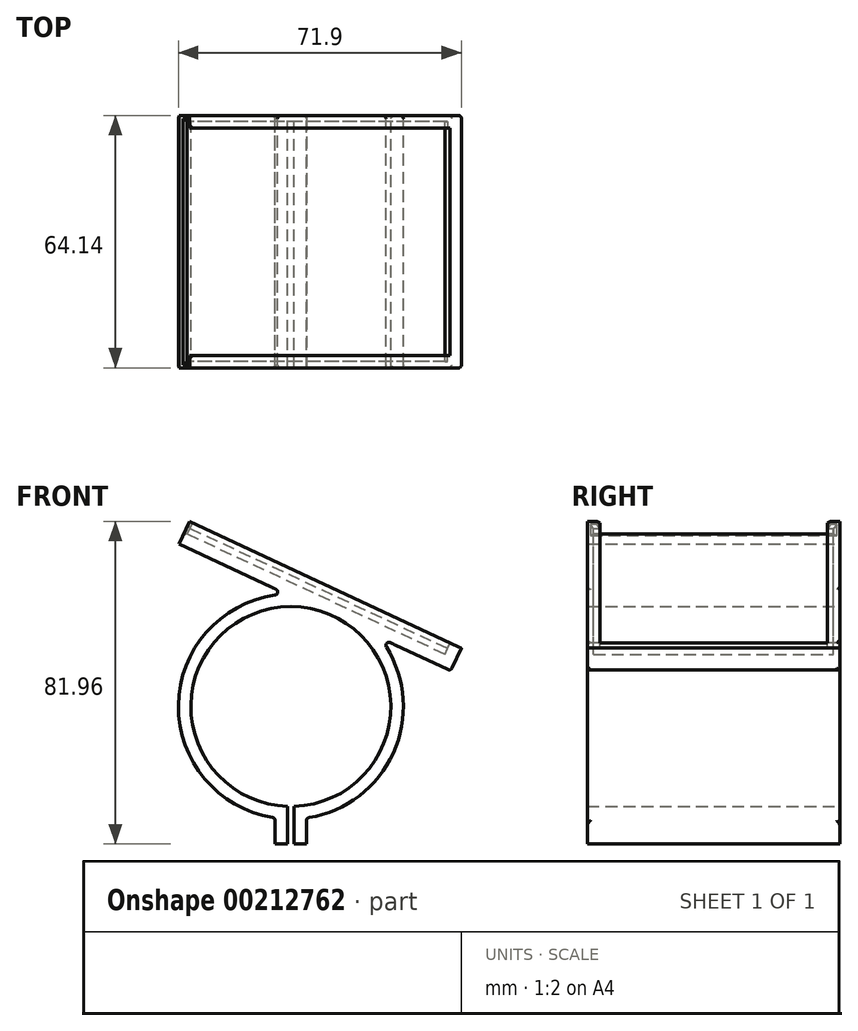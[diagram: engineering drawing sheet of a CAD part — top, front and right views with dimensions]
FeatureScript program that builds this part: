
annotation { "Feature Type Name" : "Feature", "Feature Type Description" : "" }
export const myFeature = defineFeature(function(context is Context, id is Id, definition is map)
    precondition{}
    {
        {
            var Q0;
            Q0=qCreatedBy(makeId("Front.planeOp"),FACE);
            var sketch = newSketch(context, id + "F0", { "sketchPlane" : qUnion([Q0])});
            skArc(sketch, "E0", {"start": v(0.8, -25.39) * mm, "mid": v(0, 25.4) * mm, "end": v(-0.8, -25.39) * mm});
            skArc(sketch, "E1.0", {"start": v(0.8, -28.56) * mm, "mid": v(0, 28.58) * mm, "end": v(-0.8, -28.56) * mm});
            skLineSegment(sketch, "E2", {"start": v(0, 0) * mm, "end": v(67.61, 0) * mm, "construction": true});
            skLineSegment(sketch, "E3", {"start": v(67.61, 0) * mm, "end": v(-41.32, 50.8) * mm, "construction": true});
            skLineSegment(sketch, "E4.0", {"start": v(40.65, 9.07) * mm, "end": v(-28.41, 41.27) * mm});
            skLineSegment(sketch, "E5", {"start": v(-28.41, 41.28) * mm, "end": v(-27.07, 44.15) * mm});
            skLineSegment(sketch, "E6", {"start": v(40.65, 9.07) * mm, "end": v(41.99, 11.95) * mm});
            skLineSegment(sketch, "E7", {"start": v(41.99, 11.95) * mm, "end": v(-27.07, 44.15) * mm});
            skLineSegment(sketch, "E8", {"start": v(0, 0) * mm, "end": v(0, -34.93) * mm, "construction": true});
            skLineSegment(sketch, "E9.0", {"start": v(0.8, 0) * mm, "end": v(0.8, -34.93) * mm});
            skLineSegment(sketch, "E10", {"start": v(0, -34.93) * mm, "end": v(0.8, -34.93) * mm, "construction": true});
            skLineSegment(sketch, "E11", {"start": v(0.8, -34.93) * mm, "end": v(3.97, -34.93) * mm});
            skLineSegment(sketch, "E12", {"start": v(3.97, -34.93) * mm, "end": v(3.97, -28.3) * mm});
            skLineSegment(sketch, "E13", {"start": v(0.8, -34.93) * mm, "end": v(0.8, -25.39) * mm, "construction": true});
            skLineSegment(sketch, "E14.MirrorCS", {"start": v(-0.8, 0) * mm, "end": v(-0.8, -34.93) * mm});
            skLineSegment(sketch, "E15.MirrorCS", {"start": v(-0.8, -34.93) * mm, "end": v(-3.97, -34.93) * mm});
            skLineSegment(sketch, "E16.MirrorCS", {"start": v(-0.8, -34.93) * mm, "end": v(-0.8, -25.39) * mm, "construction": true});
            skLineSegment(sketch, "E17.MirrorCS", {"start": v(0, -34.93) * mm, "end": v(-0.8, -34.93) * mm, "construction": true});
            skLineSegment(sketch, "E18.MirrorCS", {"start": v(-3.97, -34.93) * mm, "end": v(-3.97, -28.3) * mm});
            skSolve(sketch);
        }
        {
            var Q0;
            Q0 = qSketchRegion(id + "F0", true);
            extrude(context, id + "F1", {"entities" : qUnion([Q0]), "depth" : 64.13 * mm, "offsetDistance" : 25.4 * mm});
        }
        {
            var Q0;
            Q0=makeQuery(id+"F1.opExtrude","SWEPT_FACE",FACE,{"disambiguationData":[OSD([sQuery(id+"F0.wireOp",EDGE,"E5")])]});
            var sketch = newSketch(context, id + "F2", { "sketchPlane" : qUnion([Q0])});
            skLineSegment(sketch, "E19", {"start": v(0, 28.58) * mm, "end": v(0, 31.75) * mm});
            skLineSegment(sketch, "E20", {"start": v(0, 31.75) * mm, "end": v(3.18, 31.75) * mm});
            skLineSegment(sketch, "E21", {"start": v(3.18, 31.75) * mm, "end": v(3.18, 30.16) * mm});
            skLineSegment(sketch, "E22", {"start": v(3.18, 30.16) * mm, "end": v(1.59, 30.16) * mm});
            skPoint(sketch, "E22.endSnap0", {"position": v(1.59, 31.75) * mm});
            skLineSegment(sketch, "E23", {"start": v(1.59, 30.16) * mm, "end": v(1.59, 28.58) * mm});
            skLineSegment(sketch, "E24", {"start": v(32.07, 28.58) * mm, "end": v(32.07, 32.24) * mm, "construction": true});
            skLineSegment(sketch, "E25.MirrorCS", {"start": v(62.55, 30.16) * mm, "end": v(62.55, 28.58) * mm});
            skLineSegment(sketch, "E26.MirrorCS", {"start": v(64.13, 31.75) * mm, "end": v(60.96, 31.75) * mm});
            skPoint(sketch, "E27.MirrorP", {"position": v(62.55, 31.75) * mm});
            skLineSegment(sketch, "E28.MirrorCS", {"start": v(60.96, 30.16) * mm, "end": v(62.55, 30.16) * mm});
            skLineSegment(sketch, "E29.MirrorCS", {"start": v(60.96, 31.75) * mm, "end": v(60.96, 30.16) * mm});
            skLineSegment(sketch, "E30.MirrorCS", {"start": v(64.13, 28.58) * mm, "end": v(64.13, 31.75) * mm});
            skSolve(sketch);
        }
        {
            var Q0;
            {var subQ0=sQuery(id+"F2.wireOp",EDGE,"E19");Q0=makeQuery(id+"F2.imprint","IMPRINT",FACE,{"disambiguationData":[TD([[makeQuery(id+"F2.imprint","IMPRINT",EDGE,{"derivedFrom":subQ0}),-1.0]])]});}
            var Q1;
            {var subQ0=sQuery(id+"F2.wireOp",EDGE,"E25.MirrorCS");Q1=makeQuery(id+"F2.imprint","IMPRINT",FACE,{"disambiguationData":[TD([[makeQuery(id+"F2.imprint","IMPRINT",EDGE,{"derivedFrom":subQ0}),1.0]])]});}
            var Q2;
            Q2=makeQuery(id+"F1.opExtrude","SWEPT_FACE",FACE,{"disambiguationData":[OSD([sQuery(id+"F0.wireOp",EDGE,"E6")])]});
            extrude(context, id + "F3", {"entities" : qUnion([Q0, Q1]), "operationType" : NewBodyOperationType.ADD, "endBound" : BoundingType.UP_TO_SURFACE, "oppositeDirection" : true, "depth" : 25.4 * mm, "endBoundEntityFace" : qUnion([Q2]), "offsetDistance" : 25.4 * mm});
        }
        {
            var Q0;
            {var subQ0=sQuery(id+"F0.wireOp",EDGE,"E6");Q0=makeQuery(id+"F3.boolean.opBoolean","MERGE",FACE,{"derivedFrom":[makeQuery(id+"F1.opExtrude","SWEPT_FACE",FACE,{"disambiguationData":[OSD([subQ0])]}),makeQuery(id+"F3.opExtrude","CAP_FACE",FACE,{"disambiguationData":[OSD([subQ0]),OD(0.0)],"isStart":false}),makeQuery(id+"F3.opExtrude","CAP_FACE",FACE,{"disambiguationData":[OSD([subQ0]),OD(1.0)],"isStart":false})]});}
            var sketch = newSketch(context, id + "F4", { "sketchPlane" : qUnion([Q0])});
            skLineSegment(sketch, "E31", {"start": v(-60.96, 31.75) * mm, "end": v(-3.18, 31.75) * mm});
            skSolve(sketch);
        }
        {
            var Q0;
            Q0=makeQuery(id+"F4.imprint","IMPRINT",FACE,{"disambiguationData":[TD([[makeQuery(id+"F4.imprint","IMPRINT",EDGE,{"derivedFrom":sQuery(id+"F4.wireOp",EDGE,"E31")}),-1.0]])]});
            extrude(context, id + "F5", {"entities" : qUnion([Q0]), "operationType" : NewBodyOperationType.ADD, "oppositeDirection" : true, "depth" : 3.17 * mm, "offsetDistance" : 25.4 * mm});
        }
        {
            var Q0;
            {var subQ0=sQuery(id+"F0.wireOp",EDGE,"E1.0");Q0=makeQuery(id+"F1.opExtrude","CAP_EDGE",EDGE,{"disambiguationData":[OSD([subQ0]),TDD([makeQuery(id+"F0.imprint","IMPRINT",EDGE,{"disambiguationData":[TD([[makeQuery(id+"F0.imprint","INTERSECT",VERTEX,{"derivedFrom":[subQ0,sQuery(id+"F0.wireOp",EDGE,"E18.MirrorCS")]}),1.0]])],"derivedFrom":subQ0})])],"isStart":true});}
            var Q1;
            {var subQ0=sQuery(id+"F0.wireOp",EDGE,"E1.0");Q1=makeQuery(id+"F1.opExtrude","CAP_EDGE",EDGE,{"disambiguationData":[OSD([subQ0]),TDD([makeQuery(id+"F0.imprint","IMPRINT",EDGE,{"disambiguationData":[TD([[makeQuery(id+"F0.imprint","INTERSECT",VERTEX,{"derivedFrom":[subQ0,sQuery(id+"F0.wireOp",EDGE,"E18.MirrorCS")]}),1.0]])],"derivedFrom":subQ0})])],"isStart":false});}
            var Q2;
            {var subQ0=sQuery(id+"F0.wireOp",EDGE,"E4.0");var subQ1=sQuery(id+"F0.wireOp",EDGE,"E1.0");Q2=makeQuery(id+"F1.opExtrude","SWEPT_EDGE",EDGE,{"disambiguationData":[OSD([subQ1,subQ0]),TDD([makeQuery(id+"F0.imprint","INTERSECT",VERTEX,{"disambiguationData":[OD(1.0)],"derivedFrom":[subQ1,subQ0]})])]});}
            var Q3;
            {var subQ0=sQuery(id+"F0.wireOp",EDGE,"E1.0");Q3=makeQuery(id+"F1.opExtrude","SWEPT_FACE",FACE,{"disambiguationData":[OSD([subQ0]),TDD([makeQuery(id+"F0.imprint","IMPRINT",EDGE,{"disambiguationData":[TD([[makeQuery(id+"F0.imprint","INTERSECT",VERTEX,{"derivedFrom":[subQ0,sQuery(id+"F0.wireOp",EDGE,"E18.MirrorCS")]}),1.0]])],"derivedFrom":subQ0})])]});}
            var Q4;
            {var subQ0=sQuery(id+"F0.wireOp",EDGE,"E4.0");var subQ1=sQuery(id+"F0.wireOp",EDGE,"E1.0");Q4=makeQuery(id+"F1.opExtrude","SWEPT_EDGE",EDGE,{"disambiguationData":[OSD([subQ1,subQ0]),TDD([makeQuery(id+"F0.imprint","INTERSECT",VERTEX,{"disambiguationData":[OD(0.0)],"derivedFrom":[subQ1,subQ0]})])]});}
            var Q5;
            Q5=makeQuery(id+"F1.opExtrude","SWEPT_EDGE",EDGE,{"disambiguationData":[OSD([sQuery(id+"F0.wireOp",EDGE,"E1.0"),sQuery(id+"F0.wireOp",EDGE,"E12")])]});
            var Q6;
            {var subQ0=sQuery(id+"F0.wireOp",EDGE,"E1.0");Q6=makeQuery(id+"F1.opExtrude","CAP_EDGE",EDGE,{"disambiguationData":[OSD([subQ0]),TDD([makeQuery(id+"F0.imprint","IMPRINT",EDGE,{"disambiguationData":[TD([[makeQuery(id+"F0.imprint","INTERSECT",VERTEX,{"derivedFrom":[subQ0,sQuery(id+"F0.wireOp",EDGE,"E12")]}),-1.0]])],"derivedFrom":subQ0})])],"isStart":true});}
            var Q7;
            {var subQ0=sQuery(id+"F0.wireOp",EDGE,"E1.0");Q7=makeQuery(id+"F1.opExtrude","CAP_EDGE",EDGE,{"disambiguationData":[OSD([subQ0]),TDD([makeQuery(id+"F0.imprint","IMPRINT",EDGE,{"disambiguationData":[TD([[makeQuery(id+"F0.imprint","INTERSECT",VERTEX,{"derivedFrom":[subQ0,sQuery(id+"F0.wireOp",EDGE,"E12")]}),-1.0]])],"derivedFrom":subQ0})])],"isStart":false});}
            var Q8;
            {var subQ0=sQuery(id+"F0.wireOp",EDGE,"E6");Q8=makeQuery(id+"F3.boolean.opBoolean","MERGE",EDGE,{"derivedFrom":[makeQuery(id+"F1.opExtrude","CAP_EDGE",EDGE,{"disambiguationData":[OSD([subQ0])],"isStart":true}),makeQuery(id+"F3.opExtrude","TWEAK_EDGE",EDGE,{"derivedFrom":[makeQuery(id+"F1.opExtrude","SWEPT_FACE",FACE,{"disambiguationData":[OSD([subQ0])]}),makeQuery(id+"F2.imprint","IMPRINT",EDGE,{"derivedFrom":sQuery(id+"F2.wireOp",EDGE,"E19")})]})]});}
            var Q9;
            Q9=makeQuery(id+"F1.opExtrude","SWEPT_EDGE",EDGE,{"disambiguationData":[OSD([sQuery(id+"F0.wireOp",EDGE,"E4.0"),sQuery(id+"F0.wireOp",EDGE,"E6")])]});
            var Q10;
            {var subQ0=sQuery(id+"F0.wireOp",EDGE,"E6");Q10=makeQuery(id+"F3.boolean.opBoolean","MERGE",EDGE,{"derivedFrom":[makeQuery(id+"F1.opExtrude","CAP_EDGE",EDGE,{"disambiguationData":[OSD([subQ0])],"isStart":false}),makeQuery(id+"F3.opExtrude","TWEAK_EDGE",EDGE,{"derivedFrom":[makeQuery(id+"F1.opExtrude","SWEPT_FACE",FACE,{"disambiguationData":[OSD([subQ0])]}),makeQuery(id+"F2.imprint","IMPRINT",EDGE,{"derivedFrom":sQuery(id+"F2.wireOp",EDGE,"E30.MirrorCS")})]})]});}
            fillet(context, id + "F6", {"entities" : qUnion([Q0, Q1, Q2, Q3, Q4, Q5, Q6, Q7, Q8, Q9, Q10]), "radius" : 0.8 * mm, "tangentPropagation" : true, "allowEdgeOverflow" : false});
        }
        {
            var Q0;
            Q0=makeQuery(id+"F3.opExtrude","CAP_EDGE",EDGE,{"disambiguationData":[OSD([sQuery(id+"F2.wireOp",EDGE,"E22")])],"isStart":true});
            var Q1;
            Q1=makeQuery(id+"F3.opExtrude","CAP_EDGE",EDGE,{"disambiguationData":[OSD([sQuery(id+"F2.wireOp",EDGE,"E21")])],"isStart":true});
            var Q2;
            Q2=makeQuery(id+"F3.opExtrude","CAP_EDGE",EDGE,{"disambiguationData":[OSD([sQuery(id+"F2.wireOp",EDGE,"E23")])],"isStart":true});
            var Q3;
            Q3=makeQuery(id+"F1.opExtrude","SWEPT_EDGE",EDGE,{"disambiguationData":[OSD([sQuery(id+"F0.wireOp",EDGE,"E5"),sQuery(id+"F0.wireOp",EDGE,"E7")])]});
            var Q4;
            Q4=makeQuery(id+"F3.opExtrude","CAP_EDGE",EDGE,{"disambiguationData":[OSD([sQuery(id+"F2.wireOp",EDGE,"E25.MirrorCS")])],"isStart":true});
            var Q5;
            Q5=makeQuery(id+"F3.opExtrude","CAP_EDGE",EDGE,{"disambiguationData":[OSD([sQuery(id+"F2.wireOp",EDGE,"E28.MirrorCS")])],"isStart":true});
            var Q6;
            Q6=makeQuery(id+"F3.opExtrude","CAP_EDGE",EDGE,{"disambiguationData":[OSD([sQuery(id+"F2.wireOp",EDGE,"E29.MirrorCS")])],"isStart":true});
            chamfer(context, id + "F7", {"entities" : qUnion([Q0, Q1, Q2, Q3, Q4, Q5, Q6]), "width" : 0.8 * mm, "tangentPropagation" : true});
        }
    });
